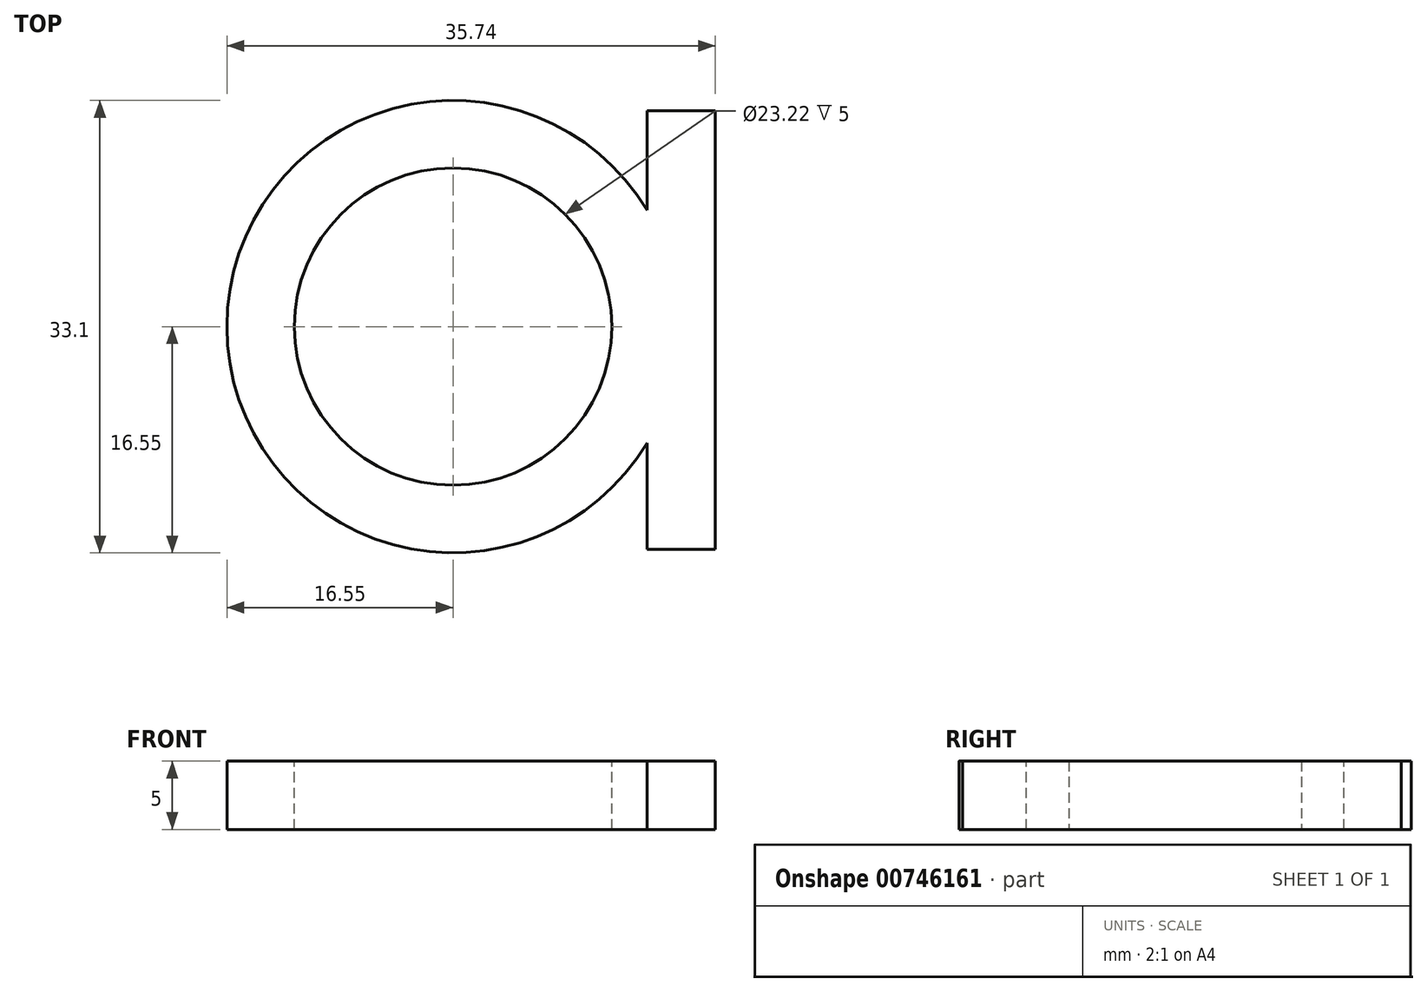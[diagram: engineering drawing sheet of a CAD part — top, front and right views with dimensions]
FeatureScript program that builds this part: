
annotation { "Feature Type Name" : "Feature", "Feature Type Description" : "" }
export const myFeature = defineFeature(function(context is Context, id is Id, definition is map)
    precondition{}
    {
        {
            var Q0;
            Q0=qCreatedBy(makeId("Top.planeOp"),FACE);
            var sketch = newSketch(context, id + "F0", { "sketchPlane" : qUnion([Q0])});
            skCircle(sketch, "E0", {"center": v(0, 0) * mm, "radius": 16.55 * mm});
            skSolve(sketch);
        }
        {
            var Q0;
            Q0 = qSketchRegion(id + "F0", true);
            extrude(context, id + "F1", {"entities" : qUnion([Q0]), "depth" : 5 * mm, "offsetDistance" : 25.4 * mm});
        }
        {
            var Q0;
            Q0=makeQuery(id+"F1.opExtrude","CAP_FACE",FACE,{"disambiguationData":[OSD([sQuery(id+"F0.wireOp",EDGE,"E0")])],"isStart":false});
            var sketch = newSketch(context, id + "F2", { "sketchPlane" : qUnion([Q0])});
            skCircle(sketch, "E1", {"center": v(0, 0) * mm, "radius": 11.61 * mm});
            skSolve(sketch);
        }
        {
            var Q0;
            Q0=makeQuery(id+"F2.imprint","IMPRINT",FACE,{"disambiguationData":[TD([[makeQuery(id+"F2.imprint","IMPRINT",EDGE,{"derivedFrom":sQuery(id+"F2.wireOp",EDGE,"E1")}),1.0]])]});
            extrude(context, id + "F3", {"entities" : qUnion([Q0]), "operationType" : NewBodyOperationType.REMOVE, "oppositeDirection" : true, "depth" : 5 * mm, "offsetDistance" : 25.4 * mm});
        }
        {
            var Q0;
            Q0=qCreatedBy(makeId("Top.planeOp"),FACE);
            var sketch = newSketch(context, id + "F4", { "sketchPlane" : qUnion([Q0])});
            skLineSegment(sketch, "E2.bottom", {"start": v(14.19, 15.8) * mm, "end": v(19.19, 15.8) * mm});
            skLineSegment(sketch, "E2.top", {"start": v(14.19, -16.3) * mm, "end": v(19.19, -16.3) * mm});
            skLineSegment(sketch, "E2.left", {"start": v(14.19, 15.8) * mm, "end": v(14.19, -16.3) * mm});
            skLineSegment(sketch, "E2.right", {"start": v(19.19, 15.8) * mm, "end": v(19.19, -16.3) * mm});
            skSolve(sketch);
        }
        {
            var Q0;
            Q0=makeQuery(id+"F4.imprint","IMPRINT",FACE,{"disambiguationData":[TD([[makeQuery(id+"F4.imprint","IMPRINT",EDGE,{"derivedFrom":sQuery(id+"F4.wireOp",EDGE,"E2.bottom")}),-1.0]])]});
            var Q1;
            Q1 = qSketchRegion(id + "F4", true);
            extrude(context, id + "F5", {"entities" : qUnion([Q0, Q1]), "operationType" : NewBodyOperationType.ADD, "depth" : 5 * mm, "offsetDistance" : 25.4 * mm});
        }
    });
